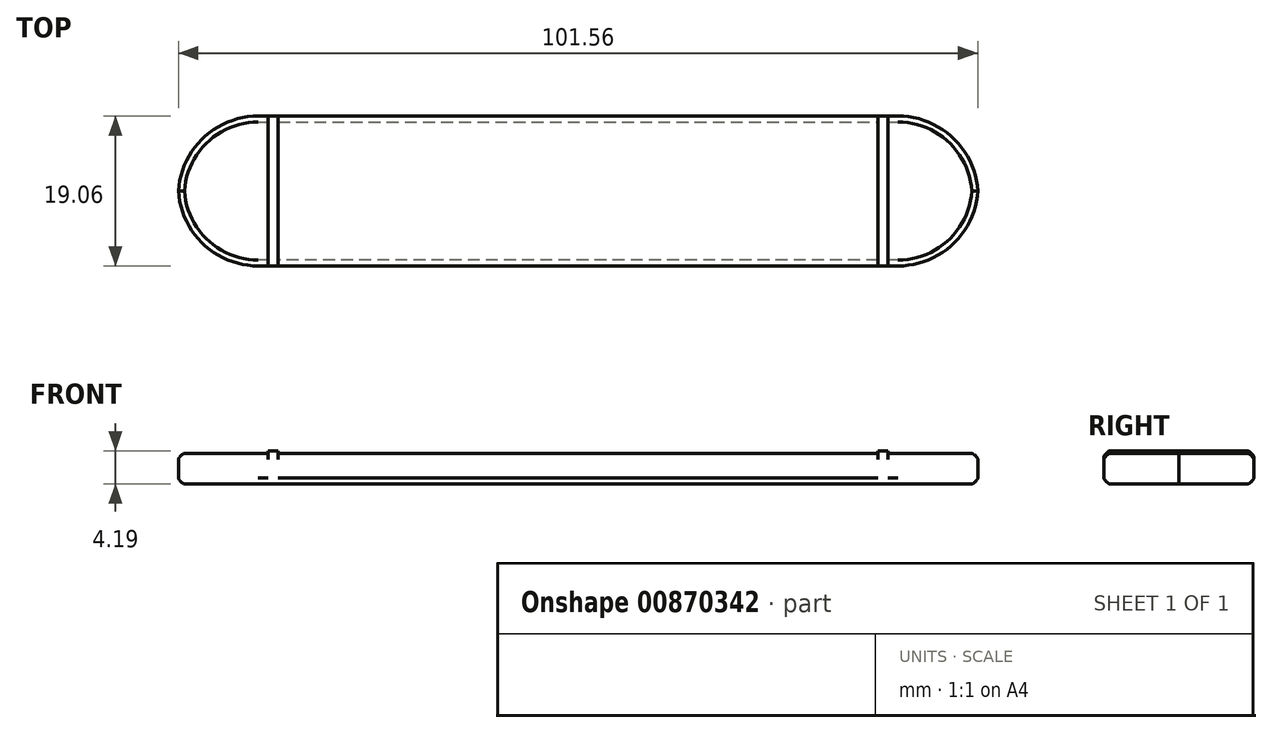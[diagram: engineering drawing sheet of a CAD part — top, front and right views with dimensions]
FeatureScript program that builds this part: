
annotation { "Feature Type Name" : "Feature", "Feature Type Description" : "" }
export const myFeature = defineFeature(function(context is Context, id is Id, definition is map)
    precondition{}
    {
        {
            var Q0;
            Q0=qCreatedBy(makeId("Top.planeOp"),FACE);
            var sketch = newSketch(context, id + "F0", { "sketchPlane" : qUnion([Q0])});
            skLineSegment(sketch, "E0.bottom", {"start": v(-50.8, 9.52) * mm, "end": v(50.8, 9.52) * mm});
            skLineSegment(sketch, "E0.top", {"start": v(-50.8, -9.53) * mm, "end": v(50.8, -9.53) * mm});
            skLineSegment(sketch, "E0.left", {"start": v(-50.8, 9.52) * mm, "end": v(-50.8, -9.53) * mm});
            skLineSegment(sketch, "E0.right", {"start": v(50.8, 9.52) * mm, "end": v(50.8, -9.53) * mm});
            skPoint(sketch, "E0.middle", {"position": v(0, 0) * mm});
            skLineSegment(sketch, "E1", {"start": v(-39.37, 9.53) * mm, "end": v(-39.37, -9.53) * mm});
            skLineSegment(sketch, "E2", {"start": v(-38.1, 9.53) * mm, "end": v(-38.1, -9.53) * mm});
            skLineSegment(sketch, "E3.MirrorCS", {"start": v(38.1, 9.53) * mm, "end": v(38.1, -9.53) * mm});
            skLineSegment(sketch, "E4.MirrorCS", {"start": v(39.37, 9.53) * mm, "end": v(39.37, -9.53) * mm});
            skSolve(sketch);
        }
        {
            var Q0;
            Q0=makeQuery(id+"F0.imprint","IMPRINT",FACE,{"disambiguationData":[TD([[makeQuery(id+"F0.imprint","IMPRINT",EDGE,{"derivedFrom":sQuery(id+"F0.wireOp",EDGE,"E0.bottom")}),-1.0]])]});
            extrude(context, id + "F1", {"entities" : qUnion([Q0]), "depth" : 3.9 * mm, "offsetDistance" : 25.4 * mm});
        }
        {
            var Q0;
            Q0=makeQuery(id+"F1.opExtrude","SWEPT_EDGE",EDGE,{"disambiguationData":[OSD([sQuery(id+"F0.wireOp",EDGE,"E0.top"),sQuery(id+"F0.wireOp",EDGE,"E0.left")])]});
            var Q1;
            Q1=makeQuery(id+"F1.opExtrude","SWEPT_EDGE",EDGE,{"disambiguationData":[OSD([sQuery(id+"F0.wireOp",EDGE,"E0.bottom"),sQuery(id+"F0.wireOp",EDGE,"E0.left")])]});
            var Q2;
            Q2=makeQuery(id+"F1.opExtrude","SWEPT_EDGE",EDGE,{"disambiguationData":[OSD([sQuery(id+"F0.wireOp",EDGE,"E0.top"),sQuery(id+"F0.wireOp",EDGE,"E0.right")])]});
            var Q3;
            Q3=makeQuery(id+"F1.opExtrude","SWEPT_EDGE",EDGE,{"disambiguationData":[OSD([sQuery(id+"F0.wireOp",EDGE,"E0.bottom"),sQuery(id+"F0.wireOp",EDGE,"E0.right")])]});
            fillet(context, id + "F2", {"entities" : qUnion([Q0, Q1, Q2, Q3]), "radius" : 10.16 * mm, "allowEdgeOverflow" : false});
        }
        {
            var Q0;
            Q0=makeQuery(id+"F1.opExtrude","CAP_EDGE",EDGE,{"disambiguationData":[OSD([sQuery(id+"F0.wireOp",EDGE,"E0.top")])],"isStart":false});
            var Q1;
            Q1=makeQuery(id+"F1.opExtrude","CAP_EDGE",EDGE,{"disambiguationData":[OSD([sQuery(id+"F0.wireOp",EDGE,"E0.top")])],"isStart":true});
            var Q2;
            {var subQ0=sQuery(id+"F0.wireOp",EDGE,"E0.right");var subQ1=sQuery(id+"F0.wireOp",EDGE,"E0.bottom");Q2=makeQuery(id+"F2.opFillet","BLEND_EDGE",EDGE,{"blendedFrom":[makeQuery(id+"F1.opExtrude","SWEPT_EDGE",EDGE,{"disambiguationData":[OSD([subQ1,subQ0])]}),makeQuery(id+"F1.opExtrude","CAP_FACE",FACE,{"disambiguationData":[OSD([subQ1,sQuery(id+"F0.wireOp",EDGE,"E0.top"),sQuery(id+"F0.wireOp",EDGE,"E0.left"),subQ0])],"isStart":true})],"blendedInto":[makeQuery(id+"F1.opExtrude","CAP_FACE",FACE,{"disambiguationData":[OSD([subQ1,sQuery(id+"F0.wireOp",EDGE,"E0.top"),sQuery(id+"F0.wireOp",EDGE,"E0.left"),subQ0])],"isStart":true})]});}
            var Q3;
            Q3=makeQuery(id+"F1.opExtrude","CAP_EDGE",EDGE,{"disambiguationData":[OSD([sQuery(id+"F0.wireOp",EDGE,"E0.bottom")])],"isStart":false});
            fillet(context, id + "F3", {"entities" : qUnion([Q0, Q1, Q2, Q3]), "radius" : 0.76 * mm, "tangentPropagation" : true, "rho" : .2, "crossSection" : FilletCrossSection.CONIC, "allowEdgeOverflow" : false});
        }
        {
            var Q0;
            {var subQ0=sQuery(id+"F0.wireOp",EDGE,"E1");Q0=makeQuery(id+"F0.imprint","IMPRINT",FACE,{"disambiguationData":[TD([[makeQuery(id+"F0.imprint","IMPRINT",EDGE,{"derivedFrom":subQ0}),1.0]])]});}
            var Q1;
            {var subQ0=sQuery(id+"F0.wireOp",EDGE,"E3.MirrorCS");Q1=makeQuery(id+"F0.imprint","IMPRINT",FACE,{"disambiguationData":[TD([[makeQuery(id+"F0.imprint","IMPRINT",EDGE,{"derivedFrom":subQ0}),1.0]])]});}
            extrude(context, id + "F4", {"entities" : qUnion([Q0, Q1]), "operationType" : NewBodyOperationType.ADD, "depth" : 4.2 * mm, "offsetDistance" : 25.4 * mm});
        }
        {
            var Q0;
            {var subQ0=sQuery(id+"F0.wireOp",EDGE,"E0.bottom");Q0=makeQuery(id+"F4.opExtrude","CAP_EDGE",EDGE,{"disambiguationData":[OSD([subQ0]),TDD([makeQuery(id+"F0.imprint","IMPRINT",EDGE,{"disambiguationData":[TD([[makeQuery(id+"F0.imprint","INTERSECT",VERTEX,{"derivedFrom":[subQ0,sQuery(id+"F0.wireOp",EDGE,"E1")]}),-1.0]])],"derivedFrom":subQ0})])],"isStart":false});}
            var Q1;
            {var subQ0=sQuery(id+"F0.wireOp",EDGE,"E0.bottom");Q1=makeQuery(id+"F4.opExtrude","CAP_EDGE",EDGE,{"disambiguationData":[OSD([subQ0]),TDD([makeQuery(id+"F0.imprint","IMPRINT",EDGE,{"disambiguationData":[TD([[makeQuery(id+"F0.imprint","INTERSECT",VERTEX,{"derivedFrom":[subQ0,sQuery(id+"F0.wireOp",EDGE,"E1")]}),-1.0]])],"derivedFrom":subQ0})])],"isStart":true});}
            var Q2;
            {var subQ0=sQuery(id+"F0.wireOp",EDGE,"E0.top");Q2=makeQuery(id+"F4.opExtrude","CAP_EDGE",EDGE,{"disambiguationData":[OSD([subQ0]),TDD([makeQuery(id+"F0.imprint","IMPRINT",EDGE,{"disambiguationData":[TD([[makeQuery(id+"F0.imprint","INTERSECT",VERTEX,{"derivedFrom":[subQ0,sQuery(id+"F0.wireOp",EDGE,"E1")]}),-1.0]])],"derivedFrom":subQ0})])],"isStart":false});}
            var Q3;
            {var subQ0=sQuery(id+"F0.wireOp",EDGE,"E0.top");Q3=makeQuery(id+"F4.opExtrude","CAP_EDGE",EDGE,{"disambiguationData":[OSD([subQ0]),TDD([makeQuery(id+"F0.imprint","IMPRINT",EDGE,{"disambiguationData":[TD([[makeQuery(id+"F0.imprint","INTERSECT",VERTEX,{"derivedFrom":[subQ0,sQuery(id+"F0.wireOp",EDGE,"E1")]}),-1.0]])],"derivedFrom":subQ0})])],"isStart":true});}
            var Q4;
            {var subQ0=sQuery(id+"F0.wireOp",EDGE,"E0.top");Q4=makeQuery(id+"F4.opExtrude","CAP_EDGE",EDGE,{"disambiguationData":[OSD([subQ0]),TDD([makeQuery(id+"F0.imprint","IMPRINT",EDGE,{"disambiguationData":[TD([[makeQuery(id+"F0.imprint","INTERSECT",VERTEX,{"derivedFrom":[subQ0,sQuery(id+"F0.wireOp",EDGE,"E3.MirrorCS")]}),-1.0]])],"derivedFrom":subQ0})])],"isStart":false});}
            var Q5;
            {var subQ0=sQuery(id+"F0.wireOp",EDGE,"E0.top");Q5=makeQuery(id+"F4.opExtrude","CAP_EDGE",EDGE,{"disambiguationData":[OSD([subQ0]),TDD([makeQuery(id+"F0.imprint","IMPRINT",EDGE,{"disambiguationData":[TD([[makeQuery(id+"F0.imprint","INTERSECT",VERTEX,{"derivedFrom":[subQ0,sQuery(id+"F0.wireOp",EDGE,"E3.MirrorCS")]}),-1.0]])],"derivedFrom":subQ0})])],"isStart":true});}
            var Q6;
            {var subQ0=sQuery(id+"F0.wireOp",EDGE,"E0.bottom");Q6=makeQuery(id+"F4.opExtrude","CAP_EDGE",EDGE,{"disambiguationData":[OSD([subQ0]),TDD([makeQuery(id+"F0.imprint","IMPRINT",EDGE,{"disambiguationData":[TD([[makeQuery(id+"F0.imprint","INTERSECT",VERTEX,{"derivedFrom":[subQ0,sQuery(id+"F0.wireOp",EDGE,"E3.MirrorCS")]}),-1.0]])],"derivedFrom":subQ0})])],"isStart":true});}
            var Q7;
            {var subQ0=sQuery(id+"F0.wireOp",EDGE,"E0.bottom");Q7=makeQuery(id+"F4.opExtrude","CAP_EDGE",EDGE,{"disambiguationData":[OSD([subQ0]),TDD([makeQuery(id+"F0.imprint","IMPRINT",EDGE,{"disambiguationData":[TD([[makeQuery(id+"F0.imprint","INTERSECT",VERTEX,{"derivedFrom":[subQ0,sQuery(id+"F0.wireOp",EDGE,"E3.MirrorCS")]}),-1.0]])],"derivedFrom":subQ0})])],"isStart":false});}
            fillet(context, id + "F5", {"entities" : qUnion([Q0, Q1, Q2, Q3, Q4, Q5, Q6, Q7]), "radius" : 0.75 * mm, "tangentPropagation" : true, "rho" : .2, "crossSection" : FilletCrossSection.CONIC, "allowEdgeOverflow" : false});
        }
    });
